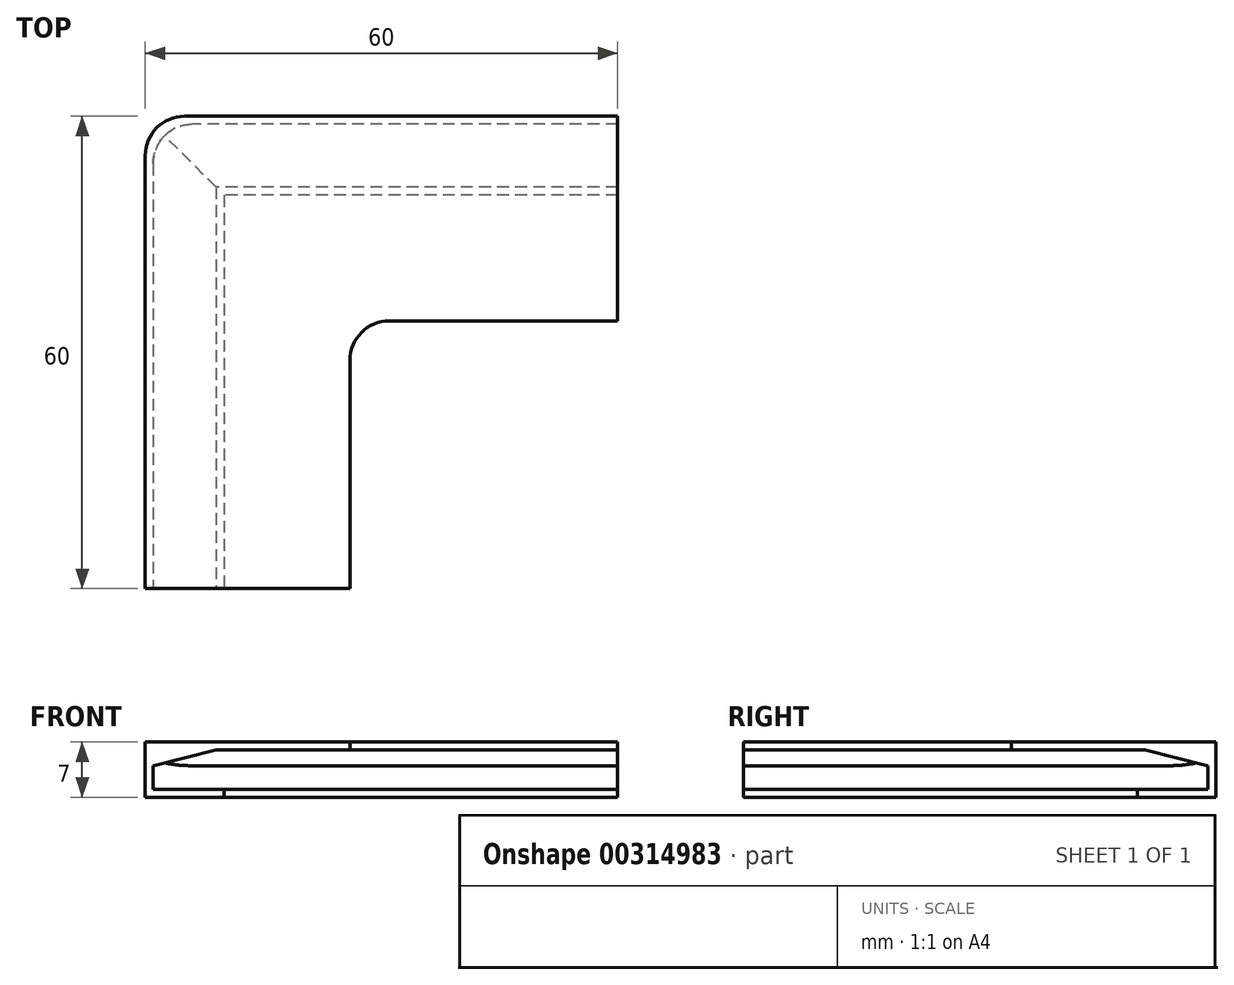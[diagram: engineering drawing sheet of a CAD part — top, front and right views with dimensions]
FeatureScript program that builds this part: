
annotation { "Feature Type Name" : "Feature", "Feature Type Description" : "" }
export const myFeature = defineFeature(function(context is Context, id is Id, definition is map)
    precondition{}
    {
        {
            var Q0;
            Q0=qCreatedBy(makeId("Right.planeOp"),FACE);
            var sketch = newSketch(context, id + "F0", { "sketchPlane" : qUnion([Q0])});
            skLineSegment(sketch, "E0", {"start": v(-24.34, 7) * mm, "end": v(1.66, 7) * mm});
            skLineSegment(sketch, "E1", {"start": v(1.66, 7) * mm, "end": v(1.66, 0) * mm});
            skLineSegment(sketch, "E2", {"start": v(1.66, 0) * mm, "end": v(-8.34, 0) * mm});
            skLineSegment(sketch, "E3", {"start": v(-24.34, 7) * mm, "end": v(-24.34, 6) * mm});
            skLineSegment(sketch, "E4", {"start": v(-24.34, 6) * mm, "end": v(-7.34, 6) * mm});
            skLineSegment(sketch, "E5", {"start": v(0.66, 4) * mm, "end": v(0.66, 1) * mm});
            skLineSegment(sketch, "E6", {"start": v(0.66, 1) * mm, "end": v(-8.34, 1) * mm});
            skLineSegment(sketch, "E7", {"start": v(-8.34, 1) * mm, "end": v(-8.34, 0) * mm});
            skLineSegment(sketch, "E8", {"start": v(-7.34, 6) * mm, "end": v(0.66, 4) * mm});
            skPoint(sketch, "E9.orphan", {"position": v(0.66, 6) * mm});
            skSolve(sketch);
        }
        {
            var Q0;
            Q0=qCreatedBy(makeId("Top.planeOp"),FACE);
            var sketch = newSketch(context, id + "F1", { "sketchPlane" : qUnion([Q0])});
            skLineSegment(sketch, "E10", {"start": v(0, 1.66) * mm, "end": v(-60, 1.66) * mm});
            skLineSegment(sketch, "E11", {"start": v(-60, 1.66) * mm, "end": v(-60, -58.34) * mm});
            skSolve(sketch);
        }
        {
            var Q0;
            Q0=makeQuery(id+"F0.imprint","IMPRINT",FACE,{"disambiguationData":[TD([[makeQuery(id+"F0.imprint","IMPRINT",EDGE,{"derivedFrom":sQuery(id+"F0.wireOp",EDGE,"E0")}),-1.0]])]});
            var Q1;
            Q1=sQuery(id+"F1.wireOp",EDGE,"E10");
            var Q2;
            Q2=sQuery(id+"F1.wireOp",EDGE,"E11");
            sweep(context, id + "F2", {"profiles" : qUnion([Q0]), "path" : qUnion([Q1, Q2])});
        }
        {
            var Q0;
            Q0=makeQuery(id+"F2.opSweep","MID_CAP_EDGE",EDGE,{"disambiguationData":[OSD([sQuery(id+"F0.wireOp",EDGE,"E5"),sQuery(id+"F1.wireOp",VERTEX,"E11.start")])],"capPos":1.0});
            fillet(context, id + "F3", {"entities" : qUnion([Q0]), "radius" : 5 * mm, "tangentPropagation" : true, "allowEdgeOverflow" : false});
        }
        {
            var Q0;
            Q0=makeQuery(id+"F2.opSweep","MID_CAP_EDGE",EDGE,{"disambiguationData":[OSD([sQuery(id+"F0.wireOp",EDGE,"E3"),sQuery(id+"F1.wireOp",VERTEX,"E11.start")])],"capPos":1.0});
            var Q1;
            Q1=makeQuery(id+"F2.opSweep","MID_CAP_EDGE",EDGE,{"disambiguationData":[OSD([sQuery(id+"F0.wireOp",EDGE,"E1"),sQuery(id+"F1.wireOp",VERTEX,"E11.start")])],"capPos":1.0});
            fillet(context, id + "F4", {"entities" : qUnion([Q0, Q1]), "radius" : 5 * mm, "tangentPropagation" : true, "allowEdgeOverflow" : false});
        }
    });
